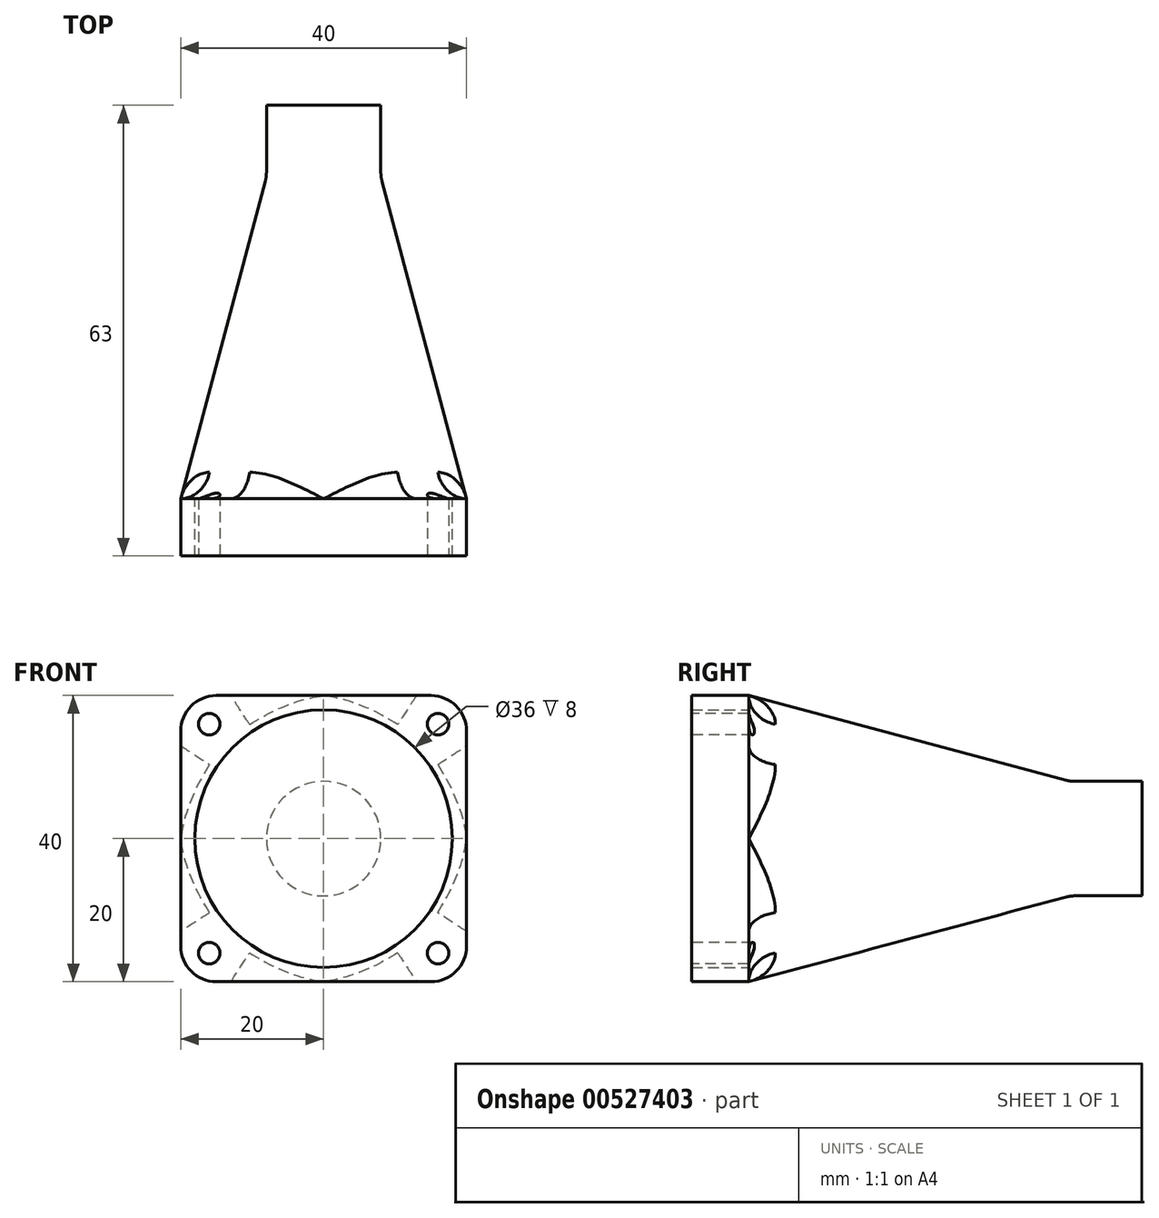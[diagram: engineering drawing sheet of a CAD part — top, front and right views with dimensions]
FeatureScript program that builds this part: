
annotation { "Feature Type Name" : "Feature", "Feature Type Description" : "" }
export const myFeature = defineFeature(function(context is Context, id is Id, definition is map)
    precondition{}
    {
        {
            var Q0;
            Q0=qCreatedBy(makeId("Front.planeOp"),FACE);
            var sketch = newSketch(context, id + "F0", { "sketchPlane" : qUnion([Q0])});
            skLineSegment(sketch, "E0.bottom", {"start": v(20, -20) * mm, "end": v(-20, -20) * mm});
            skLineSegment(sketch, "E0.top", {"start": v(20, 20) * mm, "end": v(-20, 20) * mm});
            skLineSegment(sketch, "E0.left", {"start": v(20, -20) * mm, "end": v(20, 20) * mm});
            skLineSegment(sketch, "E0.right", {"start": v(-20, -20) * mm, "end": v(-20, 20) * mm});
            skPoint(sketch, "E0.middle", {"position": v(0, 0) * mm});
            skCircle(sketch, "E1", {"center": v(0, 0) * mm, "radius": 18 * mm});
            skSolve(sketch);
        }
        {
            var Q0;
            Q0=makeQuery(id+"F0.imprint","IMPRINT",FACE,{"disambiguationData":[TD([[makeQuery(id+"F0.imprint","IMPRINT",EDGE,{"derivedFrom":sQuery(id+"F0.wireOp",EDGE,"E0.bottom")}),-1.0]])]});
            extrude(context, id + "F1", {"entities" : qUnion([Q0]), "depth" : 8 * mm, "offsetDistance" : 25 * mm});
        }
        {
            var Q0;
            Q0=qCreatedBy(makeId("Top.planeOp"),FACE);
            var sketch = newSketch(context, id + "F2", { "sketchPlane" : qUnion([Q0])});
            skLineSegment(sketch, "E2", {"start": v(0, 0) * mm, "end": v(-20, 0) * mm});
            skLineSegment(sketch, "E3", {"start": v(-20, 0) * mm, "end": v(-8, 45) * mm});
            skLineSegment(sketch, "E4", {"start": v(-8, 45) * mm, "end": v(0, 45) * mm});
            skLineSegment(sketch, "E5", {"start": v(0, 45) * mm, "end": v(0, 0) * mm});
            skLineSegment(sketch, "E6", {"start": v(0, 0) * mm, "end": v(-18, 0) * mm});
            skLineSegment(sketch, "E7", {"start": v(-18, 0) * mm, "end": v(-6, 45) * mm});
            skLineSegment(sketch, "E8", {"start": v(-6, 45) * mm, "end": v(0, 45) * mm});
            skSolve(sketch);
        }
        {
            var Q0;
            Q0=makeQuery(id+"F2.imprint","IMPRINT",FACE,{"disambiguationData":[TD([[makeQuery(id+"F2.imprint","IMPRINT",EDGE,{"derivedFrom":sQuery(id+"F2.wireOp",EDGE,"E2")}),-1.0]])]});
            var Q1;
            Q1=sQuery(id+"F2.wireOp",EDGE,"E5");
            revolve(context, id + "F3", {"operationType" : NewBodyOperationType.ADD, "entities" : qUnion([Q0]), "axis" : qUnion([Q1]), "revolveType" : RevolveType.FULL});
        }
        {
            var Q0;
            Q0=makeQuery(id+"F3.opRevolve","SWEPT_FACE",FACE,{"disambiguationData":[OSD([sQuery(id+"F2.wireOp",EDGE,"E4")])]});
            extrude(context, id + "F4", {"entities" : qUnion([Q0]), "operationType" : NewBodyOperationType.ADD, "depth" : 10 * mm, "offsetDistance" : 25 * mm});
        }
        {
            var Q0;
            {var subQ0=sQuery(id+"F2.wireOp",EDGE,"E4");var subQ1=sQuery(id+"F2.wireOp",EDGE,"E3");Q0=makeQuery(id+"F4.boolean.opBoolean","MERGE",EDGE,{"derivedFrom":[makeQuery(id+"F3.opRevolve","SWEPT_EDGE",EDGE,{"disambiguationData":[OSD([subQ1,subQ0])]}),makeQuery(id+"F4.opExtrude","CAP_EDGE",EDGE,{"disambiguationData":[OSD([subQ1,subQ0])],"isStart":true})]});}
            var Q1;
            {var subQ0=sQuery(id+"F0.wireOp",EDGE,"E0.right");var subQ1=sQuery(id+"F0.wireOp",EDGE,"E0.top");var subQ2=sQuery(id+"F2.wireOp",EDGE,"E3");Q1=makeQuery(id+"F3.boolean.opBoolean","SPLIT",EDGE,{"disambiguationData":[TD([makeQuery(id+"F1.opExtrude","CAP_FACE",FACE,{"disambiguationData":[OSD([sQuery(id+"F0.wireOp",EDGE,"E0.bottom"),subQ1,sQuery(id+"F0.wireOp",EDGE,"E0.left"),subQ0,sQuery(id+"F0.wireOp",EDGE,"E1")])],"isStart":true}),makeQuery(id+"F1.opExtrude","SWEPT_FACE",FACE,{"disambiguationData":[OSD([subQ1])]}),makeQuery(id+"F1.opExtrude","SWEPT_FACE",FACE,{"disambiguationData":[OSD([subQ0])]}),makeQuery(id+"F3.opRevolve","SWEPT_FACE",FACE,{"disambiguationData":[OSD([subQ2])]})])],"derivedFrom":makeQuery(id+"F3.opRevolve","SWEPT_EDGE",EDGE,{"disambiguationData":[OSD([sQuery(id+"F2.wireOp",EDGE,"E2"),subQ2])]})});}
            fillet(context, id + "F5", {"entities" : qUnion([Q0, Q1]), "radius" : 5 * mm, "tangentPropagation" : true, "allowEdgeOverflow" : false});
        }
        {
            var Q0;
            Q0=makeQuery(id+"F1.opExtrude","CAP_FACE",FACE,{"disambiguationData":[OSD([sQuery(id+"F0.wireOp",EDGE,"E0.bottom"),sQuery(id+"F0.wireOp",EDGE,"E0.top"),sQuery(id+"F0.wireOp",EDGE,"E0.left"),sQuery(id+"F0.wireOp",EDGE,"E0.right"),sQuery(id+"F0.wireOp",EDGE,"E1")])],"isStart":false});
            var sketch = newSketch(context, id + "F6", { "sketchPlane" : qUnion([Q0])});
            skPoint(sketch, "E9", {"position": v(-16, 16) * mm});
            skPoint(sketch, "E10.MirrorP", {"position": v(-16, -16) * mm});
            skPoint(sketch, "E11.MirrorP", {"position": v(16, -16) * mm});
            skPoint(sketch, "E12.MirrorP", {"position": v(16, 16) * mm});
            skSolve(sketch);
        }
        {
            var Q0;
            Q0=sQuery(id+"F6.wireOp",VERTEX,"E9");
            var Q1;
            Q1=sQuery(id+"F6.wireOp",VERTEX,"E12.MirrorP");
            var Q2;
            Q2=sQuery(id+"F6.wireOp",VERTEX,"E11.MirrorP");
            var Q3;
            Q3=sQuery(id+"F6.wireOp",VERTEX,"E10.MirrorP");
            var Q4;
            Q4=makeQuery(id+"F1.opExtrude","SWEPT_BODY",BODY,{"disambiguationData":[OSD([sQuery(id+"F0.wireOp",EDGE,"E0.bottom"),sQuery(id+"F0.wireOp",EDGE,"E0.top"),sQuery(id+"F0.wireOp",EDGE,"E0.left"),sQuery(id+"F0.wireOp",EDGE,"E0.right"),sQuery(id+"F0.wireOp",EDGE,"E1")])]});
            hole(context, id + "F7", {"style" : HoleStyle.SIMPLE, "endStyle" : HoleEndStyle.THROUGH, "holeDiameter" : 3 * mm, "isTappedThrough" : true, "tappedDepth" : 12 * mm, "tapClearance" : 3, "locations" : qUnion([Q0, Q1, Q2, Q3]), "scope" : qUnion([Q4])});
        }
        {
            var Q0;
            Q0=makeQuery(id+"F1.opExtrude","SWEPT_EDGE",EDGE,{"disambiguationData":[OSD([sQuery(id+"F0.wireOp",EDGE,"E0.bottom"),sQuery(id+"F0.wireOp",EDGE,"E0.left")])]});
            var Q1;
            Q1=makeQuery(id+"F1.opExtrude","SWEPT_EDGE",EDGE,{"disambiguationData":[OSD([sQuery(id+"F0.wireOp",EDGE,"E0.bottom"),sQuery(id+"F0.wireOp",EDGE,"E0.right")])]});
            var Q2;
            Q2=makeQuery(id+"F1.opExtrude","SWEPT_EDGE",EDGE,{"disambiguationData":[OSD([sQuery(id+"F0.wireOp",EDGE,"E0.top"),sQuery(id+"F0.wireOp",EDGE,"E0.right")])]});
            var Q3;
            Q3=makeQuery(id+"F1.opExtrude","SWEPT_EDGE",EDGE,{"disambiguationData":[OSD([sQuery(id+"F0.wireOp",EDGE,"E0.top"),sQuery(id+"F0.wireOp",EDGE,"E0.left")])]});
            fillet(context, id + "F8", {"entities" : qUnion([Q0, Q1, Q2, Q3]), "radius" : 5 * mm, "tangentPropagation" : true, "allowEdgeOverflow" : false});
        }
    });
